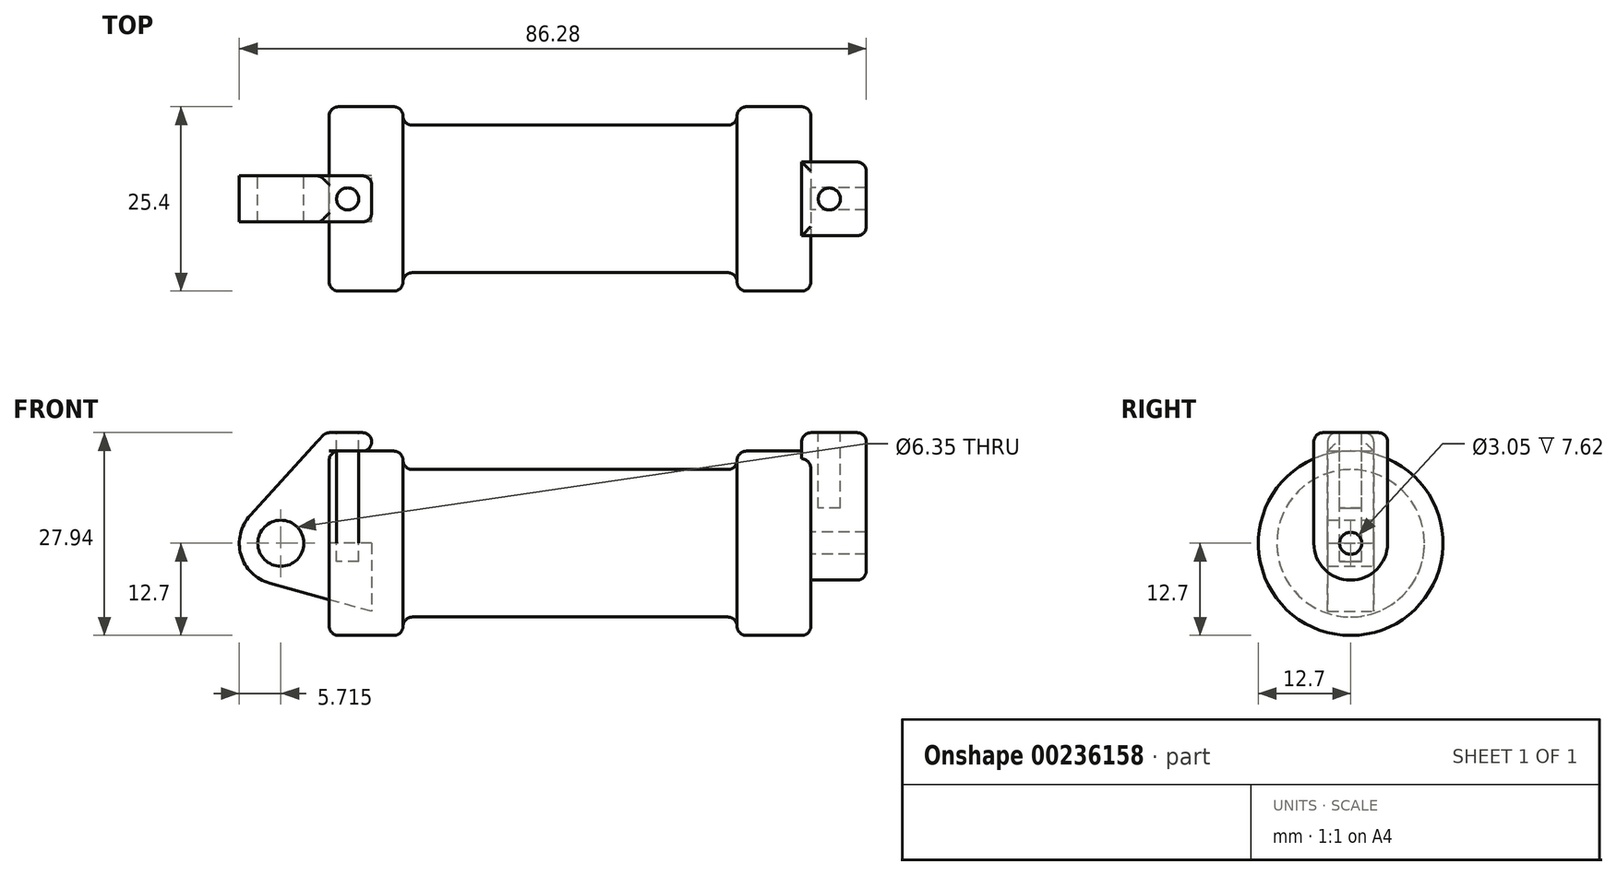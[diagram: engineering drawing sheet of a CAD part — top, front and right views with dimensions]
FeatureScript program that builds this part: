
annotation { "Feature Type Name" : "Feature", "Feature Type Description" : "" }
export const myFeature = defineFeature(function(context is Context, id is Id, definition is map)
    precondition{}
    {
        {
            var Q0;
            Q0=qCreatedBy(makeId("Front.planeOp"),FACE);
            var sketch = newSketch(context, id + "F0", { "sketchPlane" : qUnion([Q0])});
            skLineSegment(sketch, "E0", {"start": v(0, 0) * mm, "end": v(0, 12.7) * mm});
            skLineSegment(sketch, "E1", {"start": v(0, 12.7) * mm, "end": v(10.16, 12.7) * mm});
            skLineSegment(sketch, "E2", {"start": v(10.16, 12.7) * mm, "end": v(10.16, 10.16) * mm});
            skLineSegment(sketch, "E3", {"start": v(10.16, 10.16) * mm, "end": v(56.13, 10.16) * mm});
            skLineSegment(sketch, "E4", {"start": v(56.13, 10.16) * mm, "end": v(56.13, 12.7) * mm});
            skLineSegment(sketch, "E5", {"start": v(56.13, 12.7) * mm, "end": v(66.3, 12.7) * mm});
            skLineSegment(sketch, "E6", {"start": v(66.3, 12.7) * mm, "end": v(66.3, 0) * mm});
            skLineSegment(sketch, "E7", {"start": v(66.3, 0) * mm, "end": v(0, 0) * mm});
            skLineSegment(sketch, "E8", {"start": v(5.84, 15.24) * mm, "end": v(-0.5, 15.24) * mm});
            skLineSegment(sketch, "E9", {"start": v(-0.5, 15.24) * mm, "end": v(-10.88, 3.85) * mm});
            skLineSegment(sketch, "E10", {"start": v(0, 0) * mm, "end": v(-6.65, 0) * mm});
            skCircle(sketch, "E11", {"center": v(-6.65, 0) * mm, "radius": 5.72 * mm});
            skCircle(sketch, "E12", {"center": v(-6.65, 0) * mm, "radius": 3.18 * mm});
            skLineSegment(sketch, "E13", {"start": v(5.84, 15.24) * mm, "end": v(5.84, -9.4) * mm});
            skLineSegment(sketch, "E14", {"start": v(5.84, -9.4) * mm, "end": v(-8.18, -5.5) * mm});
            skSolve(sketch);
        }
        {
            var Q0;
            {var subQ0=sQuery(id+"F0.wireOp",EDGE,"E2");Q0=makeQuery(id+"F0.imprint","IMPRINT",FACE,{"disambiguationData":[TD([[makeQuery(id+"F0.imprint","IMPRINT",EDGE,{"derivedFrom":subQ0}),-1.0]])]});}
            var Q1;
            {var subQ0=sQuery(id+"F0.wireOp",EDGE,"E0");Q1=makeQuery(id+"F0.imprint","IMPRINT",FACE,{"disambiguationData":[TD([[makeQuery(id+"F0.imprint","IMPRINT",EDGE,{"derivedFrom":subQ0}),-1.0]])]});}
            var Q2;
            Q2=sQuery(id+"F0.wireOp",EDGE,"E7");
            revolve(context, id + "F1", {"entities" : qUnion([Q0, Q1]), "axis" : qUnion([Q2]), "revolveType" : RevolveType.FULL});
        }
        {
            var Q0;
            {var subQ3=sQuery(id+"F0.wireOp",EDGE,"E0");Q0=makeQuery(id+"F0.imprint","IMPRINT",FACE,{"disambiguationData":[TD([[makeQuery(id+"F0.imprint","IMPRINT",EDGE,{"derivedFrom":subQ3}),1.0]])]});}
            var Q1;
            {var subQ4=sQuery(id+"F0.wireOp",EDGE,"E12");Q1=makeQuery(id+"F0.imprint","IMPRINT",FACE,{"disambiguationData":[TD([[makeQuery(id+"F0.imprint","IMPRINT",EDGE,{"derivedFrom":subQ4}),-1.0]])]});}
            var Q2;
            {var subQ0=sQuery(id+"F0.wireOp",EDGE,"E14");Q2=makeQuery(id+"F0.imprint","IMPRINT",FACE,{"disambiguationData":[TD([[makeQuery(id+"F0.imprint","IMPRINT",EDGE,{"derivedFrom":subQ0}),-1.0]])]});}
            extrude(context, id + "F2", {"entities" : qUnion([Q0, Q1, Q2]), "endBound" : BoundingType.SYMMETRIC, "depth" : 6.35 * mm});
        }
        {
            var Q0;
            Q0=makeQuery(id+"F1.opRevolve","SWEPT_FACE",FACE,{"disambiguationData":[OSD([sQuery(id+"F0.wireOp",EDGE,"E6")])]});
            var sketch = newSketch(context, id + "F3", { "sketchPlane" : qUnion([Q0])});
            skCircle(sketch, "E15", {"center": v(0, 0) * mm, "radius": 1.52 * mm});
            skCircle(sketch, "E16", {"center": v(0, 0) * mm, "radius": 5.08 * mm});
            skLineSegment(sketch, "E17", {"start": v(-5.08, 0) * mm, "end": v(-5.08, 15.24) * mm});
            skLineSegment(sketch, "E18", {"start": v(5.08, 0) * mm, "end": v(5.08, 15.24) * mm});
            skLineSegment(sketch, "E19", {"start": v(-5.08, 15.24) * mm, "end": v(5.08, 15.24) * mm});
            skSolve(sketch);
        }
        {
            var Q0;
            {var subQ0=sQuery(id+"F3.wireOp",EDGE,"E17");var subQ1=sQuery(id+"F3.wireOp",EDGE,"E16");var subQ2=makeQuery(id+"F3.imprint","INTERSECT",VERTEX,{"derivedFrom":[subQ1,subQ0]});Q0=makeQuery(id+"F3.imprint","IMPRINT",FACE,{"disambiguationData":[TD([[makeQuery(id+"F3.imprint","IMPRINT",EDGE,{"disambiguationData":[TD([[subQ2,1.0]])],"derivedFrom":subQ1}),-1.0]])]});}
            var Q1;
            Q1=makeQuery(id+"F3.imprint","IMPRINT",FACE,{"disambiguationData":[TD([[makeQuery(id+"F3.imprint","IMPRINT",EDGE,{"derivedFrom":sQuery(id+"F3.wireOp",EDGE,"E15")}),-1.0]])]});
            var Q2;
            {var subQ0=sQuery(id+"F3.wireOp",EDGE,"E19");Q2=makeQuery(id+"F3.imprint","IMPRINT",FACE,{"disambiguationData":[TD([[makeQuery(id+"F3.imprint","IMPRINT",EDGE,{"derivedFrom":subQ0}),-1.0]])]});}
            extrude(context, id + "F4", {"entities" : qUnion([Q0, Q1, Q2]), "operationType" : NewBodyOperationType.ADD, "depth" : 7.62 * mm, "hasSecondDirection" : true, "secondDirectionOppositeDirection" : true, "secondDirectionDepth" : 1.27 * mm});
        }
        {
            var Q0;
            Q0=makeQuery(id+"F4.opExtrude","SWEPT_FACE",FACE,{"disambiguationData":[OSD([sQuery(id+"F3.wireOp",EDGE,"E19")])]});
            var sketch = newSketch(context, id + "F5", { "sketchPlane" : qUnion([Q0])});
            skCircle(sketch, "E20", {"center": v(68.83, 0) * mm, "radius": 1.52 * mm});
            skCircle(sketch, "E21", {"center": v(2.54, 0) * mm, "radius": 1.52 * mm});
            skSolve(sketch);
        }
        {
            var Q0;
            Q0=makeQuery(id+"F5.imprint","IMPRINT",FACE,{"disambiguationData":[TD([[makeQuery(id+"F5.imprint","IMPRINT",EDGE,{"derivedFrom":sQuery(id+"F5.wireOp",EDGE,"E21")}),1.0]])]});
            extrude(context, id + "F6", {"entities" : qUnion([Q0]), "oppositeDirection" : true, "depth" : 17.78 * mm});
        }
        {
            var Q0;
            Q0=makeQuery(id+"F4.opExtrude","SWEPT_FACE",FACE,{"disambiguationData":[OSD([sQuery(id+"F3.wireOp",EDGE,"E19")])]});
            var sketch = newSketch(context, id + "F7", { "sketchPlane" : qUnion([Q0])});
            skCircle(sketch, "E22", {"center": v(68.83, 0) * mm, "radius": 1.52 * mm});
            skSolve(sketch);
        }
        {
            var Q0;
            Q0=makeQuery(id+"F7.imprint","IMPRINT",FACE,{"disambiguationData":[TD([[makeQuery(id+"F7.imprint","IMPRINT",EDGE,{"derivedFrom":sQuery(id+"F7.wireOp",EDGE,"E22")}),1.0]])]});
            extrude(context, id + "F8", {"entities" : qUnion([Q0]), "oppositeDirection" : true, "depth" : 10.4 * mm});
        }
        {
            var Q0;
            Q0=makeQuery(id+"F1.opRevolve","SWEPT_EDGE",EDGE,{"disambiguationData":[OSD([sQuery(id+"F0.wireOp",EDGE,"E1"),sQuery(id+"F0.wireOp",EDGE,"E2")])]});
            var Q1;
            Q1=makeQuery(id+"F1.opRevolve","SWEPT_EDGE",EDGE,{"disambiguationData":[OSD([sQuery(id+"F0.wireOp",EDGE,"E0"),sQuery(id+"F0.wireOp",EDGE,"E1")])]});
            var Q2;
            Q2=makeQuery(id+"F2.opExtrude","SWEPT_EDGE",EDGE,{"disambiguationData":[OSD([sQuery(id+"F0.wireOp",EDGE,"E8"),sQuery(id+"F0.wireOp",EDGE,"E13")])]});
            var Q3;
            Q3=makeQuery(id+"F2.opExtrude","CAP_EDGE",EDGE,{"disambiguationData":[OSD([sQuery(id+"F0.wireOp",EDGE,"E8")])],"isStart":false});
            var Q4;
            Q4=makeQuery(id+"F2.opExtrude","SWEPT_EDGE",EDGE,{"disambiguationData":[OSD([sQuery(id+"F0.wireOp",EDGE,"E1"),sQuery(id+"F0.wireOp",EDGE,"E13")])]});
            var Q5;
            {var subQ0=sQuery(id+"F0.wireOp",EDGE,"E13");Q5=makeQuery(id+"F2.opExtrude","CAP_EDGE",EDGE,{"disambiguationData":[OSD([subQ0]),TDD([makeQuery(id+"F0.imprint","IMPRINT",EDGE,{"disambiguationData":[TD([[makeQuery(id+"F0.imprint","INTERSECT",VERTEX,{"derivedFrom":[sQuery(id+"F0.wireOp",EDGE,"E8"),subQ0]}),-1.0]])],"derivedFrom":subQ0})])],"isStart":true});}
            var Q6;
            {var subQ0=sQuery(id+"F0.wireOp",EDGE,"E13");Q6=makeQuery(id+"F2.opExtrude","CAP_EDGE",EDGE,{"disambiguationData":[OSD([subQ0]),TDD([makeQuery(id+"F0.imprint","IMPRINT",EDGE,{"disambiguationData":[TD([[makeQuery(id+"F0.imprint","INTERSECT",VERTEX,{"derivedFrom":[sQuery(id+"F0.wireOp",EDGE,"E8"),subQ0]}),-1.0]])],"derivedFrom":subQ0})])],"isStart":false});}
            var Q7;
            Q7=makeQuery(id+"F2.opExtrude","CAP_EDGE",EDGE,{"disambiguationData":[OSD([sQuery(id+"F0.wireOp",EDGE,"E8")])],"isStart":true});
            var Q8;
            Q8=makeQuery(id+"F2.opExtrude","SWEPT_EDGE",EDGE,{"disambiguationData":[OSD([sQuery(id+"F0.wireOp",EDGE,"E8"),sQuery(id+"F0.wireOp",EDGE,"E9")])]});
            var Q9;
            Q9=makeQuery(id+"F1.opRevolve","SWEPT_EDGE",EDGE,{"disambiguationData":[OSD([sQuery(id+"F0.wireOp",EDGE,"E2"),sQuery(id+"F0.wireOp",EDGE,"E3")])]});
            var Q10;
            Q10=makeQuery(id+"F1.opRevolve","SWEPT_FACE",FACE,{"disambiguationData":[OSD([sQuery(id+"F0.wireOp",EDGE,"E3")])]});
            var Q11;
            Q11=makeQuery(id+"F4.opExtrude","CAP_EDGE",EDGE,{"disambiguationData":[OSD([sQuery(id+"F3.wireOp",EDGE,"E19")])],"isStart":false});
            var Q12;
            Q12=makeQuery(id+"F4.opExtrude","SWEPT_EDGE",EDGE,{"disambiguationData":[OSD([sQuery(id+"F3.wireOp",EDGE,"E18"),sQuery(id+"F3.wireOp",EDGE,"E19")])]});
            var Q13;
            Q13=makeQuery(id+"F4.opExtrude","CAP_EDGE",EDGE,{"disambiguationData":[OSD([sQuery(id+"F3.wireOp",EDGE,"E19")])],"isStart":true});
            var Q14;
            Q14=makeQuery(id+"F4.opExtrude","SWEPT_EDGE",EDGE,{"disambiguationData":[OSD([sQuery(id+"F3.wireOp",EDGE,"E17"),sQuery(id+"F3.wireOp",EDGE,"E19")])]});
            var Q15;
            Q15=makeQuery(id+"F1.opRevolve","SWEPT_EDGE",EDGE,{"disambiguationData":[OSD([sQuery(id+"F0.wireOp",EDGE,"E4"),sQuery(id+"F0.wireOp",EDGE,"E5")])]});
            var Q16;
            Q16=makeQuery(id+"F1.opRevolve","SWEPT_EDGE",EDGE,{"disambiguationData":[OSD([sQuery(id+"F0.wireOp",EDGE,"E5"),sQuery(id+"F0.wireOp",EDGE,"E6")])]});
            var Q17;
            Q17=makeQuery(id+"F4.opExtrude","CAP_EDGE",EDGE,{"disambiguationData":[OSD([sQuery(id+"F3.wireOp",EDGE,"E17")])],"isStart":false});
            var Q18;
            Q18=makeQuery(id+"F4.opExtrude","CAP_EDGE",EDGE,{"disambiguationData":[OSD([sQuery(id+"F3.wireOp",EDGE,"E18")])],"isStart":false});
            var Q19;
            Q19=makeQuery(id+"F4.opExtrude","CAP_EDGE",EDGE,{"disambiguationData":[OSD([sQuery(id+"F3.wireOp",EDGE,"E16")])],"isStart":false});
            fillet(context, id + "F9", {"entities" : qUnion([Q0, Q1, Q2, Q3, Q4, Q5, Q6, Q7, Q8, Q9, Q10, Q11, Q12, Q13, Q14, Q15, Q16, Q17, Q18, Q19]), "radius" : 1.27 * mm, "tangentPropagation" : true, "allowEdgeOverflow" : false});
        }
    });
